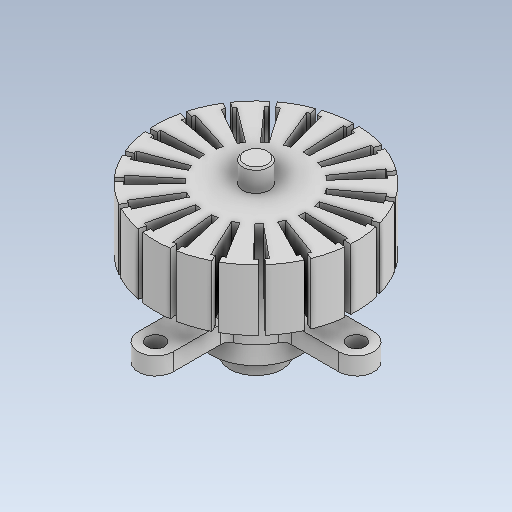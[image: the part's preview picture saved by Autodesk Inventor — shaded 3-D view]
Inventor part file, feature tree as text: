
AUTODESK INVENTOR PART (.ipt)
format: ipt  version: 2023 (Build 270158000, 158)  size: 388,608 bytes
history: native  units: mm
features: sketch x8, extrude x7, projected_geometry x3, hole x1, fillet x1, pattern_circular x1, plane x1, chamfer x1
ambient origin geometry x8: Origin, YZ Plane, XZ Plane, XY Plane, X Axis, Y Axis, Z Axis, Center Point
bodies: Solid1 (feature_tree)
feature tree (23):
  extrude  "Extrusion1"  Depth=5.0mm TaperAngle=0.0deg
  extrude  "Extrusion2"  Depth=2.5mm TaperAngle=0.0deg
  extrude  "Extrusion3"  Depth=1.7mm TaperAngle=0.0deg
  extrude  "Extrusion4"  Depth=11.5mm
  hole  "Hole1"  [1 undecoded]
  fillet  "Fillet1"  Radius=23.0mm
  extrude  "Extrusion5"  Depth=2.0mm TaperAngle=0.0deg
  extrude  "Extrusion6"  Depth=1.0mm
  pattern_circular  "Circular Pattern1"  [2 undecoded]
  sketch  "Sketch8"  dims[d25=6.0mm d26=4.2mm d27=0.0mm d28=23.0mm d29=1.047198mm d30=1.047198mm d31=0.8mm d32=0.349066mm d33=0.349066mm d34=7.0mm d35=0.0mm d36=190.0mm d37=360.0deg d39=3.0mm d40=7.0mm d41=0.0mm d42=0.2mm d43=2.0mm d44=45.0deg]
  plane  "Work Plane1"
  extrude  "Extrusion7"  Depth=2.0mm
  chamfer  "Chamfer1"  Distance=1.047198mm
  sketch  "Sketch1"  dims[d0=11.5mm d1=5.0mm d2=0.0mm]
  sketch  "Sketch2"  dims[d3=10.3mm d4=2.5mm d5=0.0mm]
  sketch  "Sketch3"  dims[d6=1.35mm d7=1.7mm d8=0.0mm]
  projected_geometry  "Projected Loop1"
  sketch  "Sketch4"  dims[d9=11.5mm d10=23.0mm]
  sketch  "Sketch5"  dims[d11=4.0mm d12=11.5mm d13=23.0mm]
  projected_geometry  "Projected Loop2"
  sketch  "Sketch6"  dims[d14=4.0mm d15=2.0mm d16=0.0mm]
  sketch  "Sketch7"  dims[d17=2.0mm d18=6.0mm d19=4.0mm d20=2.0mm d21=90.0deg d22=5.0mm d23=0.0mm d24=1.0mm]
  projected_geometry  "Projected Loop3"
note: 3 required parameter values undecoded (feature->parameter linkage not recoverable at this tier; creation-order binding heuristic only, values carry confidence <= 0.55)
